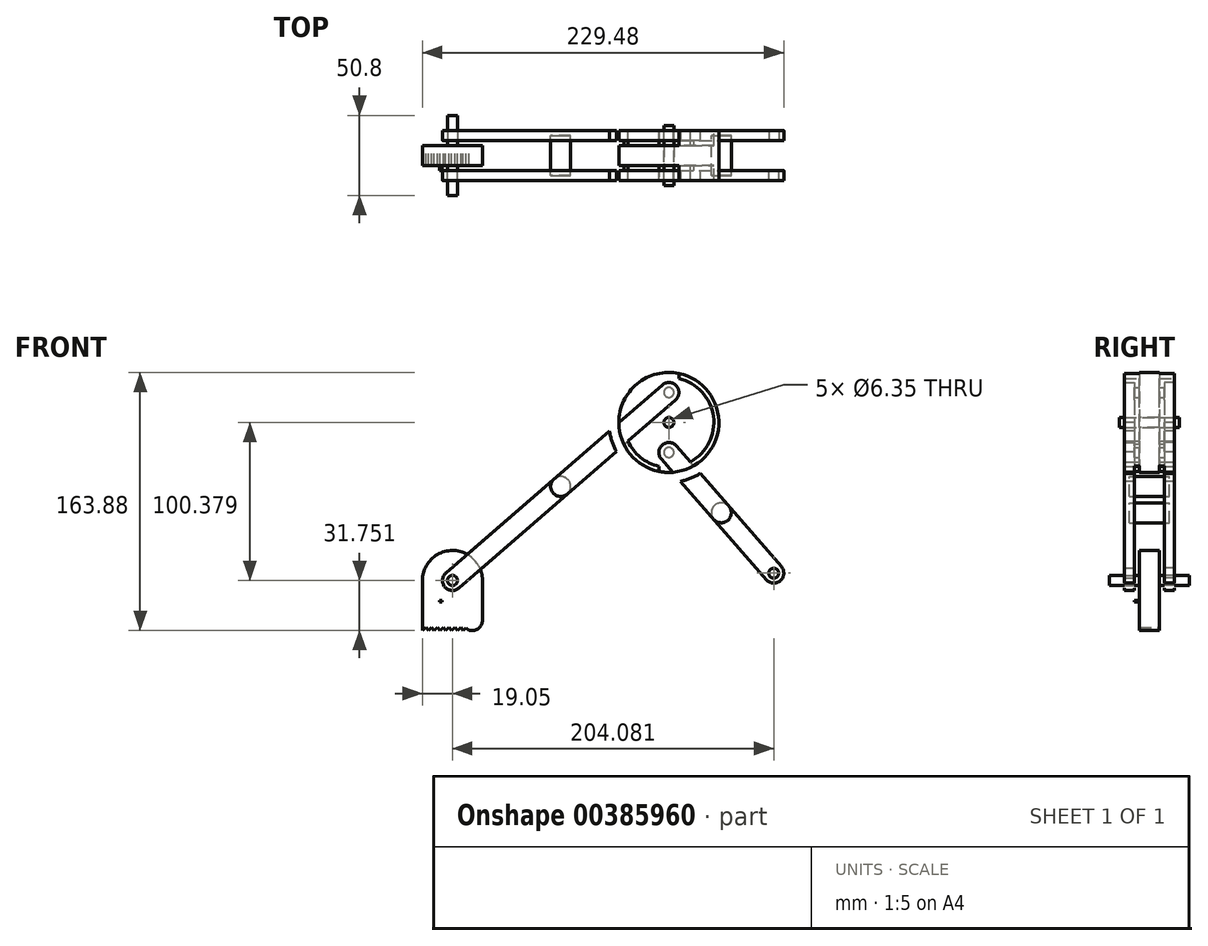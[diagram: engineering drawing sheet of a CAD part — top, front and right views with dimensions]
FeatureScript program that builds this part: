
annotation { "Feature Type Name" : "Feature", "Feature Type Description" : "" }
export const myFeature = defineFeature(function(context is Context, id is Id, definition is map)
    precondition{}
    {
        {
            var Q0;
            Q0=qCreatedBy(makeId("Front.planeOp"),FACE);
            var sketch = newSketch(context, id + "F0", { "sketchPlane" : qUnion([Q0])});
            skCircle(sketch, "E0", {"center": v(0, 0) * mm, "radius": 38.1 * mm});
            skSolve(sketch);
        }
        {
            var Q0;
            Q0 = qSketchRegion(id + "F0", true);
            extrude(context, id + "F1", {"entities" : qUnion([Q0]), "endBound" : BoundingType.SYMMETRIC, "depth" : 12.7 * mm});
        }
        {
            var Q0;
            Q0=qCreatedBy(makeId("Front.planeOp"),FACE);
            var sketch = newSketch(context, id + "F2", { "sketchPlane" : qUnion([Q0])});
            skCircle(sketch, "E1", {"center": v(0, -19.05) * mm, "radius": 3.18 * mm});
            skLineSegment(sketch, "E2", {"start": v(-15.77, 0) * mm, "end": v(14.99, 0) * mm});
            skCircle(sketch, "E3.MirrorC", {"center": v(0, 19.05) * mm, "radius": 3.18 * mm});
            skSolve(sketch);
        }
        {
            var Q0;
            Q0 = qSketchRegion(id + "F2", true);
            extrude(context, id + "F3", {"entities" : qUnion([Q0]), "operationType" : NewBodyOperationType.ADD, "endBound" : BoundingType.SYMMETRIC, "depth" : 25.4 * mm});
        }
        {
            var Q0;
            Q0=makeQuery(id+"F3.opExtrude","CAP_FACE",FACE,{"disambiguationData":[OSD([sQuery(id+"F2.wireOp",EDGE,"E1")])],"isStart":false});
            var sketch = newSketch(context, id + "F4", { "sketchPlane" : qUnion([Q0])});
            skCircle(sketch, "E4.0", {"center": v(0, 19.05) * mm, "radius": 3.18 * mm});
            skCircle(sketch, "E5.0", {"center": v(0, -19.05) * mm, "radius": 3.18 * mm});
            skArc(sketch, "E6", {"start": v(4.8, -14.88) * mm, "mid": v(-4.17, -14.26) * mm, "end": v(-4.8, -23.22) * mm});
            skArc(sketch, "E7", {"start": v(4.17, 14.26) * mm, "mid": v(4.8, 23.22) * mm, "end": v(-4.17, 23.84) * mm});
            skLineSegment(sketch, "E8", {"start": v(-4.8, -23.22) * mm, "end": v(61.85, -99.9) * mm});
            skLineSegment(sketch, "E9", {"start": v(-2.4, -21.13) * mm, "end": v(2.4, -16.97) * mm});
            skLineSegment(sketch, "E10", {"start": v(4.8, -14.88) * mm, "end": v(71.43, -91.58) * mm});
            skLineSegment(sketch, "E11", {"start": v(28.53, -61.56) * mm, "end": v(19.46, -69.44) * mm});
            skCircle(sketch, "E12.MirrorC", {"center": v(66.64, -95.74) * mm, "radius": 3.18 * mm});
            skArc(sketch, "E13.MirrorCS", {"start": v(71.43, -91.58) * mm, "mid": v(70.8, -100.53) * mm, "end": v(61.85, -99.9) * mm});
            skLineSegment(sketch, "E14", {"start": v(0, 19.05) * mm, "end": v(2.08, 16.65) * mm});
            skLineSegment(sketch, "E15", {"start": v(2.08, 16.65) * mm, "end": v(-2.08, 21.45) * mm});
            skLineSegment(sketch, "E16", {"start": v(4.17, 14.26) * mm, "end": v(-121.81, -95.21) * mm});
            skLineSegment(sketch, "E17", {"start": v(-4.17, 23.84) * mm, "end": v(-141.6, -95.59) * mm});
            skPoint(sketch, "E18.orphan", {"position": v(-149.84, -95.74) * mm});
            skLineSegment(sketch, "E19", {"start": v(-139.52, -97.98) * mm, "end": v(-135.36, -102.78) * mm});
            skLineSegment(sketch, "E20", {"start": v(-121.81, -95.21) * mm, "end": v(-133.27, -105.17) * mm});
            skLineSegment(sketch, "E21", {"start": v(-72.89, -35.87) * mm, "end": v(-83.61, -23.53) * mm});
            skArc(sketch, "E22.MirrorC", {"start": v(-133.27, -105.17) * mm, "mid": v(-142.23, -104.54) * mm, "end": v(-141.6, -95.59) * mm});
            skCircle(sketch, "E23.MirrorC", {"center": v(-137.44, -100.38) * mm, "radius": 3.18 * mm});
            skLineSegment(sketch, "E24.trimOffspring", {"start": v(-133.27, -105.17) * mm, "end": v(-128.26, -110.94) * mm});
            skSolve(sketch);
        }
        {
            var Q0;
            {var subQ4=sQuery(id+"F4.wireOp",EDGE,"E7");Q0=makeQuery(id+"F4.imprint","IMPRINT",FACE,{"disambiguationData":[TD([[makeQuery(id+"F4.imprint","IMPRINT",EDGE,{"derivedFrom":subQ4}),1.0]])]});}
            var Q1;
            {var subQ1=sQuery(id+"F4.wireOp",EDGE,"E6");Q1=makeQuery(id+"F4.imprint","IMPRINT",FACE,{"disambiguationData":[TD([[makeQuery(id+"F4.imprint","IMPRINT",EDGE,{"derivedFrom":subQ1}),1.0]])]});}
            extrude(context, id + "F5", {"entities" : qUnion([Q0, Q1]), "endBound" : BoundingType.SYMMETRIC, "depth" : 6.35 * mm});
        }
        {
            var Q0;
            Q0=makeQuery(id+"F5.opExtrude","SWEPT_BODY",BODY,{"disambiguationData":[OSD([sQuery(id+"F4.wireOp",EDGE,"E4.0"),sQuery(id+"F4.wireOp",EDGE,"E7"),sQuery(id+"F4.wireOp",EDGE,"E16"),sQuery(id+"F4.wireOp",EDGE,"E17"),sQuery(id+"F4.wireOp",EDGE,"E20"),sQuery(id+"F4.wireOp",EDGE,"E22.MirrorC"),sQuery(id+"F4.wireOp",EDGE,"E23.MirrorC")])]});
            var Q1;
            Q1=makeQuery(id+"F5.opExtrude","SWEPT_BODY",BODY,{"disambiguationData":[OSD([sQuery(id+"F4.wireOp",EDGE,"E5.0"),sQuery(id+"F4.wireOp",EDGE,"E6"),sQuery(id+"F4.wireOp",EDGE,"E8"),sQuery(id+"F4.wireOp",EDGE,"E10"),sQuery(id+"F4.wireOp",EDGE,"E12.MirrorC"),sQuery(id+"F4.wireOp",EDGE,"E13.MirrorCS")])]});
            var Q2;
            Q2=qCreatedBy(makeId("Front.planeOp"),FACE);
            mirror(context, id + "F6", {"entities" : qUnion([Q0, Q1]), "mirrorPlane" : qUnion([Q2])});
        }
        {
            var Q0;
            Q0=qCreatedBy(makeId("Front.planeOp"),FACE);
            var sketch = newSketch(context, id + "F7", { "sketchPlane" : qUnion([Q0])});
            skLineSegment(sketch, "E25.0.0", {"start": v(-4.8, -23.22) * mm, "end": v(61.85, -99.9) * mm});
            skArc(sketch, "E25.0.1", {"start": v(61.85, -99.9) * mm, "mid": v(70.8, -100.53) * mm, "end": v(71.43, -91.58) * mm});
            skLineSegment(sketch, "E25.0.2", {"start": v(71.43, -91.58) * mm, "end": v(4.8, -14.88) * mm});
            skArc(sketch, "E25.0.3", {"start": v(4.8, -14.88) * mm, "mid": v(-4.17, -14.26) * mm, "end": v(-4.8, -23.22) * mm});
            skLineSegment(sketch, "E26", {"start": v(28.53, -61.56) * mm, "end": v(38.11, -53.23) * mm});
            skCircle(sketch, "E27", {"center": v(33.32, -57.4) * mm, "radius": 6.35 * mm});
            skSolve(sketch);
        }
        {
            var Q0;
            {var subQ0=sQuery(id+"F7.wireOp",EDGE,"E26");Q0=makeQuery(id+"F7.imprint","IMPRINT",FACE,{"disambiguationData":[TD([[makeQuery(id+"F7.imprint","IMPRINT",EDGE,{"derivedFrom":subQ0}),1.0]])]});}
            var Q1;
            {var subQ0=sQuery(id+"F7.wireOp",EDGE,"E26");Q1=makeQuery(id+"F7.imprint","IMPRINT",FACE,{"disambiguationData":[TD([[makeQuery(id+"F7.imprint","IMPRINT",EDGE,{"derivedFrom":subQ0}),-1.0]])]});}
            extrude(context, id + "F8", {"entities" : qUnion([Q0, Q1]), "endBound" : BoundingType.SYMMETRIC, "depth" : 25.4 * mm});
        }
        {
            var Q0;
            Q0=qCreatedBy(makeId("Front.planeOp"),FACE);
            var sketch = newSketch(context, id + "F9", { "sketchPlane" : qUnion([Q0])});
            skLineSegment(sketch, "E28.0.0", {"start": v(-4.17, 23.84) * mm, "end": v(-141.6, -95.59) * mm});
            skArc(sketch, "E28.0.1", {"start": v(-141.6, -95.59) * mm, "mid": v(-142.23, -104.54) * mm, "end": v(-133.27, -105.17) * mm});
            skLineSegment(sketch, "E28.0.2", {"start": v(-133.27, -105.17) * mm, "end": v(4.17, 14.26) * mm});
            skArc(sketch, "E28.0.3", {"start": v(4.17, 14.26) * mm, "mid": v(4.8, 23.22) * mm, "end": v(-4.17, 23.84) * mm});
            skLineSegment(sketch, "E29", {"start": v(-64.55, -45.46) * mm, "end": v(-72.89, -35.87) * mm});
            skCircle(sketch, "E30", {"center": v(-68.72, -40.66) * mm, "radius": 6.35 * mm});
            skSolve(sketch);
        }
        {
            var Q0;
            {var subQ0=sQuery(id+"F9.wireOp",EDGE,"E29");Q0=makeQuery(id+"F9.imprint","IMPRINT",FACE,{"disambiguationData":[TD([[makeQuery(id+"F9.imprint","IMPRINT",EDGE,{"derivedFrom":subQ0}),1.0]])]});}
            var Q1;
            {var subQ0=sQuery(id+"F9.wireOp",EDGE,"E29");Q1=makeQuery(id+"F9.imprint","IMPRINT",FACE,{"disambiguationData":[TD([[makeQuery(id+"F9.imprint","IMPRINT",EDGE,{"derivedFrom":subQ0}),-1.0]])]});}
            extrude(context, id + "F10", {"entities" : qUnion([Q0, Q1]), "endBound" : BoundingType.SYMMETRIC, "depth" : 25.4 * mm});
        }
        {
            var Q0;
            Q0=makeQuery(id+"F3.opExtrude","CAP_FACE",FACE,{"disambiguationData":[OSD([sQuery(id+"F2.wireOp",EDGE,"E3.MirrorC")])],"isStart":false});
            var sketch = newSketch(context, id + "F11", { "sketchPlane" : qUnion([Q0])});
            skCircle(sketch, "E31.0", {"center": v(0, 19.05) * mm, "radius": 3.18 * mm});
            skCircle(sketch, "E32.0", {"center": v(0, -19.05) * mm, "radius": 3.18 * mm});
            skSolve(sketch);
        }
        {
            var Q0;
            Q0 = qSketchRegion(id + "F11", true);
            var Q1;
            Q1=makeQuery(id+"F5.opExtrude","CAP_FACE",FACE,{"disambiguationData":[OSD([sQuery(id+"F4.wireOp",EDGE,"E4.0"),sQuery(id+"F4.wireOp",EDGE,"E7"),sQuery(id+"F4.wireOp",EDGE,"E16"),sQuery(id+"F4.wireOp",EDGE,"E17"),sQuery(id+"F4.wireOp",EDGE,"E20"),sQuery(id+"F4.wireOp",EDGE,"E22.MirrorC"),sQuery(id+"F4.wireOp",EDGE,"E23.MirrorC")])],"isStart":false});
            extrude(context, id + "F12", {"entities" : qUnion([Q0]), "operationType" : NewBodyOperationType.ADD, "endBound" : BoundingType.UP_TO_SURFACE, "endBoundEntityFace" : qUnion([Q1]), "depth" : 25.4 * mm});
        }
        {
            var Q0;
            Q0=makeQuery(id+"F3.opExtrude","CAP_FACE",FACE,{"disambiguationData":[OSD([sQuery(id+"F2.wireOp",EDGE,"E1")])],"isStart":true});
            var sketch = newSketch(context, id + "F13", { "sketchPlane" : qUnion([Q0])});
            skCircle(sketch, "E33.0", {"center": v(0, -19.05) * mm, "radius": 3.18 * mm});
            skCircle(sketch, "E34.0", {"center": v(0, 19.05) * mm, "radius": 3.18 * mm});
            skSolve(sketch);
        }
        {
            var Q0;
            Q0 = qSketchRegion(id + "F13", true);
            var Q1;
            Q1=makeQuery(id+"F6.opPattern","COPY",FACE,{"derivedFrom":makeQuery(id+"F5.opExtrude","CAP_FACE",FACE,{"disambiguationData":[OSD([sQuery(id+"F4.wireOp",EDGE,"E4.0"),sQuery(id+"F4.wireOp",EDGE,"E7"),sQuery(id+"F4.wireOp",EDGE,"E16"),sQuery(id+"F4.wireOp",EDGE,"E17"),sQuery(id+"F4.wireOp",EDGE,"E20"),sQuery(id+"F4.wireOp",EDGE,"E22.MirrorC"),sQuery(id+"F4.wireOp",EDGE,"E23.MirrorC")])],"isStart":false}),"instanceName":"1"});
            extrude(context, id + "F14", {"entities" : qUnion([Q0]), "operationType" : NewBodyOperationType.ADD, "endBound" : BoundingType.UP_TO_SURFACE, "endBoundEntityFace" : qUnion([Q1]), "depth" : 25.4 * mm});
        }
        {
            var Q0;
            Q0=qCreatedBy(makeId("Front.planeOp"),FACE);
            var sketch = newSketch(context, id + "F15", { "sketchPlane" : qUnion([Q0])});
            skCircle(sketch, "E35", {"center": v(0, 0) * mm, "radius": 3.18 * mm});
            skSolve(sketch);
        }
        {
            var Q0;
            Q0 = qSketchRegion(id + "F15", true);
            extrude(context, id + "F16", {"entities" : qUnion([Q0]), "operationType" : NewBodyOperationType.REMOVE, "endBound" : BoundingType.SYMMETRIC, "oppositeDirection" : true, "depth" : 127 * mm});
        }
        {
            var Q0;
            Q0=qCreatedBy(makeId("Front.planeOp"),FACE);
            var sketch = newSketch(context, id + "F17", { "sketchPlane" : qUnion([Q0])});
            skCircle(sketch, "E36.0", {"center": v(0, 0) * mm, "radius": 3.18 * mm});
            skSolve(sketch);
        }
        {
            var Q0;
            Q0 = qSketchRegion(id + "F17", true);
            extrude(context, id + "F18", {"entities" : qUnion([Q0]), "endBound" : BoundingType.SYMMETRIC, "depth" : 38.1 * mm});
        }
        {
            var Q0;
            Q0=qCreatedBy(makeId("Front.planeOp"),FACE);
            var sketch = newSketch(context, id + "F19", { "sketchPlane" : qUnion([Q0])});
            skLineSegment(sketch, "E37.0", {"start": v(13.67, -25.1) * mm, "end": v(71.43, -91.58) * mm});
            skLineSegment(sketch, "E38.0", {"start": v(-25.97, -11.93) * mm, "end": v(-133.27, -105.17) * mm});
            skArc(sketch, "E39.0", {"start": v(20.02, -32.41) * mm, "mid": v(37.4, 7.3) * mm, "end": v(6.35, 37.57) * mm});
            skArc(sketch, "E40", {"start": v(13.67, -25.1) * mm, "mid": v(28.3, 3.91) * mm, "end": v(6.35, 27.86) * mm});
            skLineSegment(sketch, "E41", {"start": v(0, 0) * mm, "end": v(-6.35, 0) * mm});
            skLineSegment(sketch, "E42", {"start": v(-6.35, -27.86) * mm, "end": v(-6.35, -37.57) * mm});
            skPoint(sketch, "E43.orphan", {"position": v(4.17, 14.26) * mm});
            skLineSegment(sketch, "E44", {"start": v(0, 0) * mm, "end": v(6.35, 0) * mm});
            skLineSegment(sketch, "E45", {"start": v(6.35, 27.86) * mm, "end": v(6.35, 37.57) * mm});
            skPoint(sketch, "E46.orphan", {"position": v(4.8, -14.88) * mm});
            skArc(sketch, "E47.trimOffspring", {"start": v(-25.97, -11.93) * mm, "mid": v(-18.02, -22.18) * mm, "end": v(-6.35, -27.86) * mm});
            skArc(sketch, "E48.trimOffspring", {"start": v(-33.38, -18.37) * mm, "mid": v(-22.06, -31.06) * mm, "end": v(-6.35, -37.57) * mm});
            skSolve(sketch);
        }
        {
            var Q0;
            Q0 = qSketchRegion(id + "F19", true);
            extrude(context, id + "F20", {"entities" : qUnion([Q0]), "operationType" : NewBodyOperationType.ADD, "endBound" : BoundingType.SYMMETRIC, "depth" : 31.75 * mm});
        }
        {
            var Q0;
            Q0=qCreatedBy(makeId("Front.planeOp"),FACE);
            var sketch = newSketch(context, id + "F21", { "sketchPlane" : qUnion([Q0])});
            skCircle(sketch, "E49.0", {"center": v(-137.44, -100.38) * mm, "radius": 3.18 * mm});
            skSolve(sketch);
        }
        {
            var Q0;
            Q0 = qSketchRegion(id + "F21", true);
            extrude(context, id + "F22", {"entities" : qUnion([Q0]), "endBound" : BoundingType.SYMMETRIC, "depth" : 50.8 * mm});
        }
        {
            var Q0;
            Q0=qCreatedBy(makeId("Front.planeOp"),FACE);
            var sketch = newSketch(context, id + "F23", { "sketchPlane" : qUnion([Q0])});
            skCircle(sketch, "E50.0.0", {"center": v(-137.44, -100.38) * mm, "radius": 3.18 * mm});
            skArc(sketch, "E51", {"start": v(-118.39, -100.38) * mm, "mid": v(-137.44, -81.33) * mm, "end": v(-156.49, -100.38) * mm});
            skLineSegment(sketch, "E52", {"start": v(-156.49, -100.38) * mm, "end": v(-156.49, -125.78) * mm});
            skLineSegment(sketch, "E53", {"start": v(-118.39, -100.38) * mm, "end": v(-118.39, -125.78) * mm});
            skCircle(sketch, "E54", {"center": v(-124.74, -125.78) * mm, "radius": 6.35 * mm});
            skLineSegment(sketch, "E55", {"start": v(-156.49, -125.78) * mm, "end": v(-156.49, -132.13) * mm});
            skLineSegment(sketch, "E56", {"start": v(-156.49, -132.13) * mm, "end": v(-154.26, -130.32) * mm});
            skLineSegment(sketch, "E57", {"start": v(-154.26, -130.32) * mm, "end": v(-152.8, -132.13) * mm});
            skLineSegment(sketch, "E58", {"start": v(-152.8, -132.13) * mm, "end": v(-150.57, -130.32) * mm});
            skLineSegment(sketch, "E59", {"start": v(-150.57, -130.32) * mm, "end": v(-149.1, -132.13) * mm});
            skLineSegment(sketch, "E60", {"start": v(-149.1, -132.13) * mm, "end": v(-146.88, -130.32) * mm});
            skLineSegment(sketch, "E61", {"start": v(-146.88, -130.32) * mm, "end": v(-145.4, -132.13) * mm});
            skLineSegment(sketch, "E62", {"start": v(-145.4, -132.13) * mm, "end": v(-143.18, -130.32) * mm});
            skLineSegment(sketch, "E63", {"start": v(-143.18, -130.32) * mm, "end": v(-141.71, -132.13) * mm});
            skLineSegment(sketch, "E64", {"start": v(-141.71, -132.13) * mm, "end": v(-139.49, -130.32) * mm});
            skLineSegment(sketch, "E65", {"start": v(-139.49, -130.32) * mm, "end": v(-138.02, -132.13) * mm});
            skLineSegment(sketch, "E66", {"start": v(-138.02, -132.13) * mm, "end": v(-135.8, -130.32) * mm});
            skLineSegment(sketch, "E67", {"start": v(-135.8, -130.32) * mm, "end": v(-134.32, -132.13) * mm});
            skLineSegment(sketch, "E68", {"start": v(-134.32, -132.13) * mm, "end": v(-132.1, -130.32) * mm});
            skLineSegment(sketch, "E69", {"start": v(-132.1, -130.32) * mm, "end": v(-130.63, -132.13) * mm});
            skLineSegment(sketch, "E70", {"start": v(-130.63, -132.13) * mm, "end": v(-128.81, -130.65) * mm});
            skLineSegment(sketch, "E71", {"start": v(-128.81, -130.65) * mm, "end": v(-127.04, -132.13) * mm});
            skLineSegment(sketch, "E72", {"start": v(-127.04, -132.13) * mm, "end": v(-124.74, -132.13) * mm});
            skLineSegment(sketch, "E73", {"start": v(-124.74, -132.13) * mm, "end": v(-128.81, -130.65) * mm});
            skSolve(sketch);
        }
        {
            var Q0;
            Q0 = qSketchRegion(id + "F23", true);
            extrude(context, id + "F24", {"entities" : qUnion([Q0]), "operationType" : NewBodyOperationType.ADD, "endBound" : BoundingType.SYMMETRIC, "depth" : 12.7 * mm});
        }
        {
            var Q0;
            Q0=makeQuery(id+"F24.opExtrude","CAP_FACE",FACE,{"disambiguationData":[OSD([sQuery(id+"F23.wireOp",EDGE,"E50.0.0"),sQuery(id+"F23.wireOp",EDGE,"E51"),sQuery(id+"F23.wireOp",EDGE,"E52"),sQuery(id+"F23.wireOp",EDGE,"E53"),sQuery(id+"F23.wireOp",EDGE,"CQjJskgZ-Y8Ag-hVgr-Dxke-kYjVzhuSrTpE"),sQuery(id+"F23.wireOp",EDGE,"beNdhifU-ftpL-Vs13-nJv1-uKfH6lIVqm1k"),sQuery(id+"F23.wireOp",EDGE,"eGuWvl7Z-iJVw-Swww-pzxK-6ldATWcHfmz6"),sQuery(id+"F23.wireOp",EDGE,"u95hX8AU-4rZL-V7JR-ZCJr-VaZJvyQgxsgv"),sQuery(id+"F23.wireOp",EDGE,"pCvprVbf-sSBP-oPoh-69VG-r1ySlBIB6r10"),sQuery(id+"F23.wireOp",EDGE,"xvN5RJYm-XxiL-KG2g-QUtW-ql2C39kDQ1vV"),sQuery(id+"F23.wireOp",EDGE,"F0Jl334O-7LzL-74md-SCE4-oXF17rSnCnle"),sQuery(id+"F23.wireOp",EDGE,"k3a8EqJm-7T6Y-LMuD-abrk-ZgG0d1wSUXd2"),sQuery(id+"F23.wireOp",EDGE,"NOxjY2eA-66Rp-1ss0-Rvqj-qZmiTSfd4TBd"),sQuery(id+"F23.wireOp",EDGE,"ajkMLcDF-gQ4n-Qdtr-F5uk-ClPcaiheg9qm"),sQuery(id+"F23.wireOp",EDGE,"ipfyEPDs-w4J4-oA4s-9AB2-VVwkzUFvwDp5"),sQuery(id+"F23.wireOp",EDGE,"Uht4y7Yc-bA7b-38ou-LbLs-zrN0GXA3LsEn"),sQuery(id+"F23.wireOp",EDGE,"ZRd0LHFL-91BI-bEZT-Uo20-9k1FCNI4B5p8"),sQuery(id+"F23.wireOp",EDGE,"IPVAXEUR-X2PR-2RnW-0HCC-GbbxDrDRxc51"),sQuery(id+"F23.wireOp",EDGE,"0Cxx8802-fMwj-08gY-4AT3-2URlElv2b83n"),sQuery(id+"F23.wireOp",EDGE,"1oz5HMhS-Id9I-KZTE-JR7N-BwQd7NIATlj5"),sQuery(id+"F23.wireOp",EDGE,"f7XdPmxy-T16r-aCqp-hgTP-3Kqh52Q74sVa"),sQuery(id+"F23.wireOp",EDGE,"lXO0KMRT-Yiko-CJIG-RSCc-CyqYvlXPu0W1")])],"isStart":false});
            var sketch = newSketch(context, id + "F25", { "sketchPlane" : qUnion([Q0])});
            skLineSegment(sketch, "E74.bottom", {"start": v(-145.71, -113.11) * mm, "end": v(-143.96, -113.11) * mm});
            skLineSegment(sketch, "E74.top", {"start": v(-145.71, -113.99) * mm, "end": v(-143.96, -113.99) * mm});
            skLineSegment(sketch, "E74.left", {"start": v(-145.71, -113.11) * mm, "end": v(-145.71, -113.99) * mm});
            skLineSegment(sketch, "E74.right", {"start": v(-143.96, -113.11) * mm, "end": v(-143.96, -113.99) * mm});
            skSolve(sketch);
        }
        {
            var Q0;
            Q0 = qSketchRegion(id + "F25", true);
            extrude(context, id + "F26", {"entities" : qUnion([Q0]), "operationType" : NewBodyOperationType.ADD, "depth" : 3.17 * mm});
        }
        {
            var Q0;
            Q0=qCreatedBy(makeId("Front.planeOp"),FACE);
            var sketch = newSketch(context, id + "F27", { "sketchPlane" : qUnion([Q0])});
            skArc(sketch, "E75.0", {"start": v(6.35, 37.57) * mm, "mid": v(-31.06, 22.06) * mm, "end": v(-33.38, -18.37) * mm});
            skArc(sketch, "E76.0", {"start": v(20.02, -32.41) * mm, "mid": v(37.4, 7.3) * mm, "end": v(6.35, 37.57) * mm});
            skArc(sketch, "E77.0", {"start": v(-6.35, -37.57) * mm, "mid": v(7.3, -37.4) * mm, "end": v(20.02, -32.41) * mm});
            skArc(sketch, "E78.0", {"start": v(-33.38, -18.37) * mm, "mid": v(-22.06, -31.06) * mm, "end": v(-6.35, -37.57) * mm});
            skCircle(sketch, "E79", {"center": v(0, 0) * mm, "radius": 31.75 * mm});
            skSolve(sketch);
        }
        {
            var Q0;
            Q0 = qSketchRegion(id + "F27", true);
            extrude(context, id + "F28", {"entities" : qUnion([Q0]), "operationType" : NewBodyOperationType.REMOVE, "endBound" : BoundingType.SYMMETRIC, "oppositeDirection" : true, "depth" : 50.8 * mm});
        }
    });
